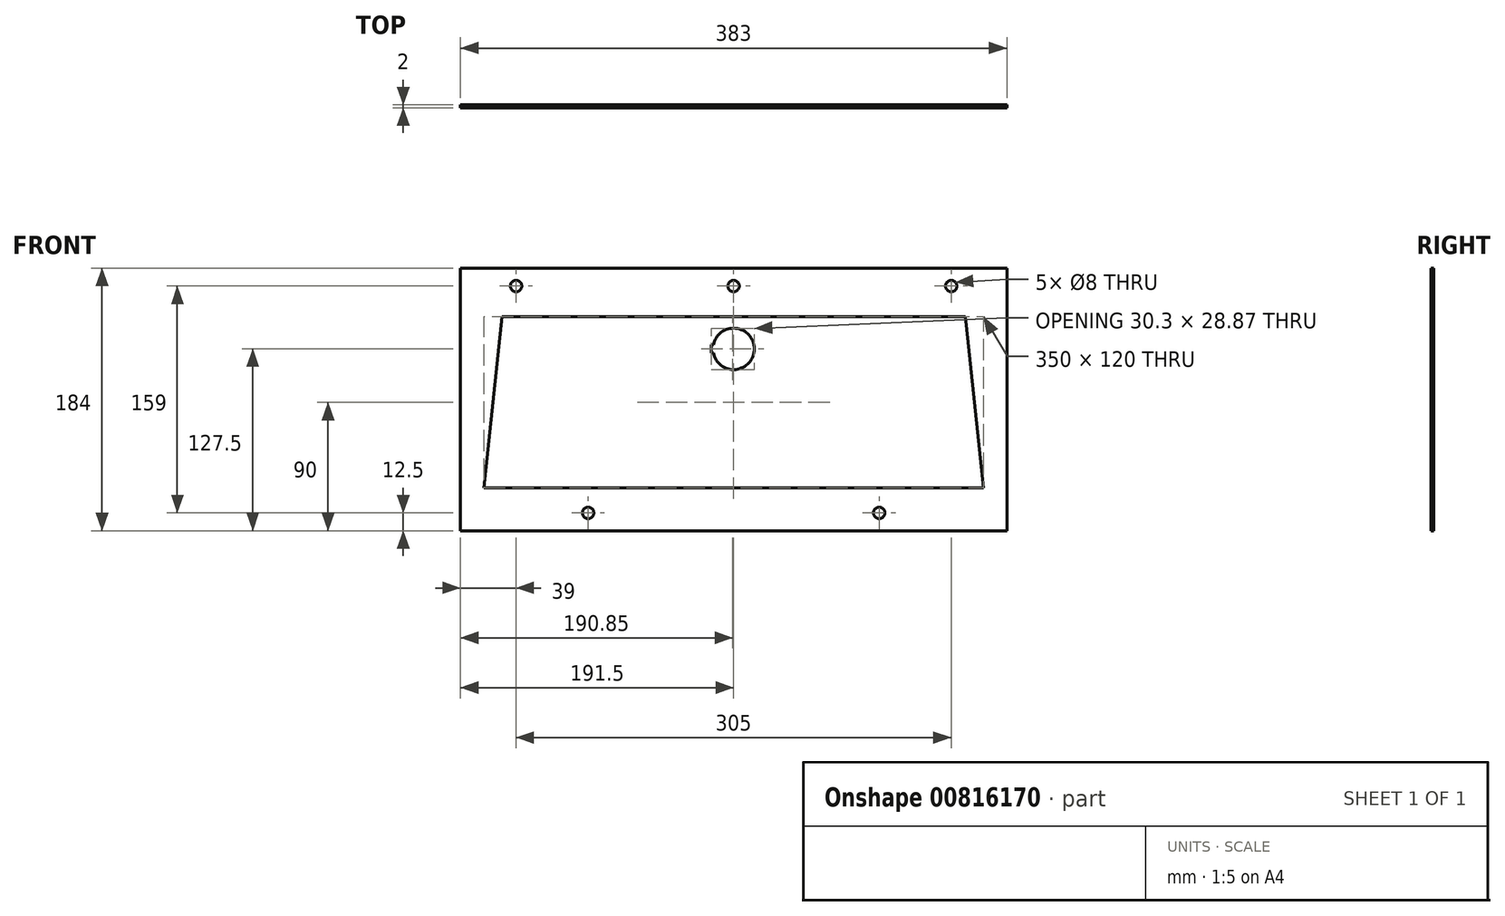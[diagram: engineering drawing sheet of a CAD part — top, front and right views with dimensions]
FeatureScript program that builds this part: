
annotation { "Feature Type Name" : "Feature", "Feature Type Description" : "" }
export const myFeature = defineFeature(function(context is Context, id is Id, definition is map)
    precondition{}
    {
        {
            var Q0;
            Q0=qCreatedBy(makeId("Front.planeOp"),FACE);
            var sketch = newSketch(context, id + "F0", { "sketchPlane" : qUnion([Q0])});
            skLineSegment(sketch, "E0.bottom", {"start": v(-191.5, 92) * mm, "end": v(191.5, 92) * mm});
            skLineSegment(sketch, "E0.top", {"start": v(-191.5, -92) * mm, "end": v(191.5, -92) * mm});
            skLineSegment(sketch, "E0.left", {"start": v(-191.5, 92) * mm, "end": v(-191.5, -92) * mm});
            skLineSegment(sketch, "E0.right", {"start": v(191.5, 92) * mm, "end": v(191.5, -92) * mm});
            skPoint(sketch, "E0.middle", {"position": v(0, 0) * mm});
            skLineSegment(sketch, "E1", {"start": v(0, 139.2) * mm, "end": v(0, -150) * mm, "construction": true});
            skCircle(sketch, "E2", {"center": v(0, 79.5) * mm, "radius": 4 * mm});
            skCircle(sketch, "E3", {"center": v(-152.5, 79.5) * mm, "radius": 4 * mm});
            skCircle(sketch, "E4", {"center": v(152.5, 79.5) * mm, "radius": 4 * mm});
            skCircle(sketch, "E5", {"center": v(102, -79.5) * mm, "radius": 4 * mm});
            skCircle(sketch, "E6", {"center": v(-102, -79.5) * mm, "radius": 4 * mm});
            skLineSegment(sketch, "E7.bottom", {"start": v(-162.5, 58) * mm, "end": v(162.5, 58) * mm});
            skLineSegment(sketch, "E7.top", {"start": v(-175, -62) * mm, "end": v(175, -62) * mm});
            skPoint(sketch, "E7.middle", {"position": v(0, 0.5) * mm});
            skLineSegment(sketch, "E8", {"start": v(-162.5, 58) * mm, "end": v(-175, -62) * mm});
            skLineSegment(sketch, "E9", {"start": v(162.5, 58) * mm, "end": v(175, -62) * mm});
            skSolve(sketch);
        }
        {
            var Q0;
            Q0=makeQuery(id+"F0.imprint","IMPRINT",FACE,{"disambiguationData":[TD([[makeQuery(id+"F0.imprint","IMPRINT",EDGE,{"derivedFrom":sQuery(id+"F0.wireOp",EDGE,"E0.bottom")}),-1.0]])]});
            var sketch = newSketch(context, id + "F1", { "sketchPlane" : qUnion([Q0])});
            skPoint(sketch, "E10.0", {"position": v(-191.5, 92) * mm});
            skPoint(sketch, "E11.0", {"position": v(191.5, -92) * mm});
            skSolve(sketch);
        }
        {
            var Q0;
            Q0=qCreatedBy(makeId("Front.planeOp"),FACE);
            var sketch = newSketch(context, id + "F2", { "sketchPlane" : qUnion([Q0])});
            skArc(sketch, "E12", {"start": v(-14.24, 32.75) * mm, "mid": v(14.5, 35.5) * mm, "end": v(-14.24, 38.25) * mm});
            skLineSegment(sketch, "E13", {"start": v(0, 35.5) * mm, "end": v(-26.04, 35.5) * mm, "construction": true});
            skLineSegment(sketch, "E14.bottom", {"start": v(-15.8, 38.25) * mm, "end": v(-14.24, 38.25) * mm});
            skLineSegment(sketch, "E14.top", {"start": v(-15.8, 32.75) * mm, "end": v(-14.24, 32.75) * mm});
            skLineSegment(sketch, "E14.left", {"start": v(-15.8, 38.25) * mm, "end": v(-15.8, 32.75) * mm});
            skSolve(sketch);
        }
        {
            var Q0;
            Q0=makeQuery(id+"F1.imprint","IMPRINT",FACE,{"disambiguationData":[TD([[makeQuery(id+"F1.imprint","IMPRINT",EDGE,{"derivedFrom":makeQuery(id+"F0.imprint","IMPRINT",EDGE,{"derivedFrom":sQuery(id+"F0.wireOp",EDGE,"E0.bottom")})}),-1.0]])]});
            var Q1;
            Q1=makeQuery(id+"F0.imprint","IMPRINT",FACE,{"disambiguationData":[TD([[makeQuery(id+"F0.imprint","IMPRINT",EDGE,{"derivedFrom":sQuery(id+"F0.wireOp",EDGE,"E7.bottom")}),-1.0]])]});
            extrude(context, id + "F3", {"entities" : qUnion([Q0, Q1]), "depth" : 2 * mm, "offsetDistance" : 25 * mm});
        }
        {
            var Q0;
            Q0 = qSketchRegion(id + "F2", true);
            extrude(context, id + "F4", {"entities" : qUnion([Q0]), "operationType" : NewBodyOperationType.REMOVE, "endBound" : BoundingType.THROUGH_ALL, "depth" : 25 * mm, "offsetDistance" : 25 * mm});
        }
    });
